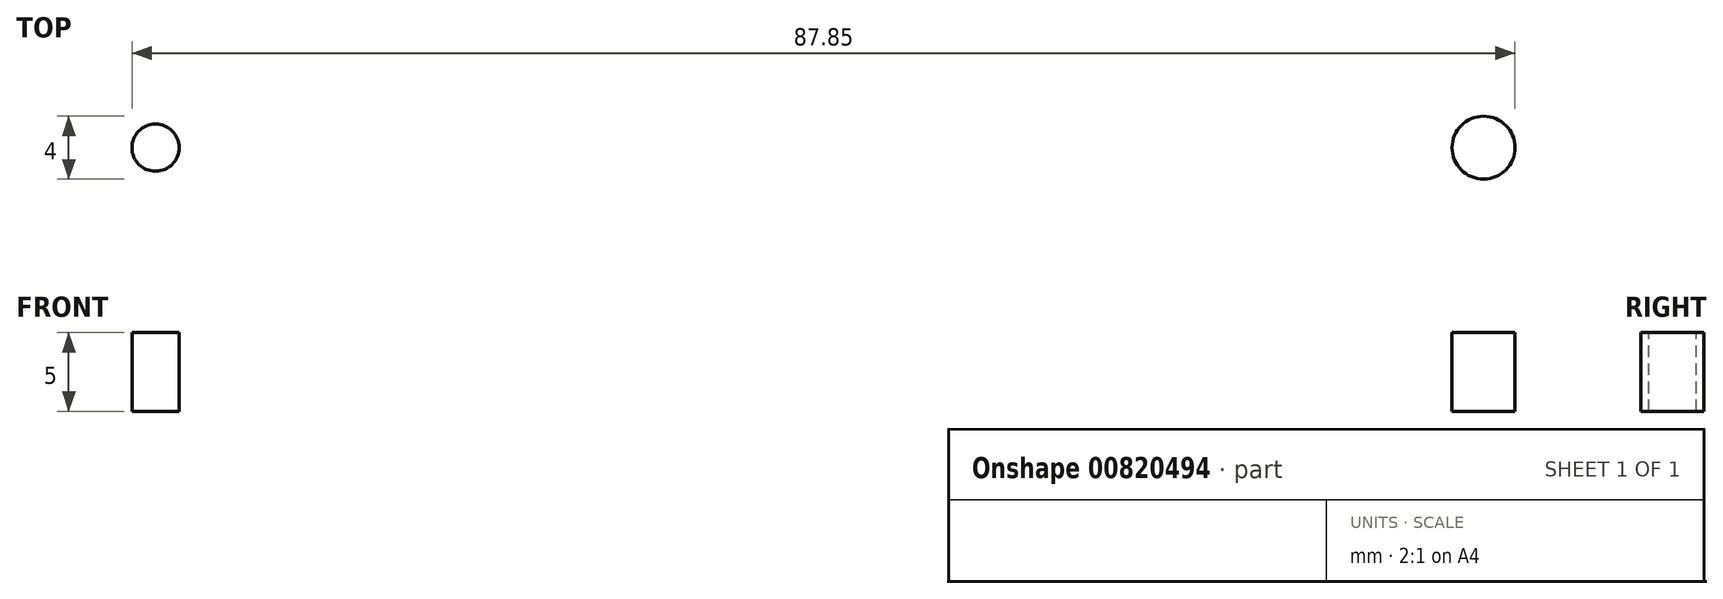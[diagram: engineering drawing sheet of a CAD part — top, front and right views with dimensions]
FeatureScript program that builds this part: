
annotation { "Feature Type Name" : "Feature", "Feature Type Description" : "" }
export const myFeature = defineFeature(function(context is Context, id is Id, definition is map)
    precondition{}
    {
        {
            var Q0;
            Q0=qCreatedBy(makeId("Top.planeOp"),FACE);
            var sketch = newSketch(context, id + "F0", { "sketchPlane" : qUnion([Q0])});
            skLineSegment(sketch, "E0.bottom", {"start": v(69.35, 12.75) * mm, "end": v(-69.35, 12.75) * mm});
            skLineSegment(sketch, "E0.top", {"start": v(69.35, -12.75) * mm, "end": v(-69.35, -12.75) * mm});
            skLineSegment(sketch, "E0.left", {"start": v(69.35, 12.75) * mm, "end": v(69.35, -12.75) * mm});
            skLineSegment(sketch, "E0.right", {"start": v(-69.35, 12.75) * mm, "end": v(-69.35, -12.75) * mm});
            skPoint(sketch, "E0.middle", {"position": v(0, 0) * mm});
            skSolve(sketch);
        }
        {
            var Q0;
            Q0=makeQuery(id+"F0.imprint","IMPRINT",FACE,{"disambiguationData":[TD([[makeQuery(id+"F0.imprint","IMPRINT",EDGE,{"derivedFrom":sQuery(id+"F0.wireOp",EDGE,"E0.bottom")}),1.0]])]});
            extrude(context, id + "F1", {"entities" : qUnion([Q0]), "depth" : 5 * mm, "offsetDistance" : 25 * mm});
        }
        {
            var Q0;
            Q0=makeQuery(id+"F1.opExtrude","CAP_FACE",FACE,{"disambiguationData":[OSD([sQuery(id+"F0.wireOp",EDGE,"E0.bottom"),sQuery(id+"F0.wireOp",EDGE,"E0.top"),sQuery(id+"F0.wireOp",EDGE,"E0.left"),sQuery(id+"F0.wireOp",EDGE,"E0.right")])],"isStart":false});
            var sketch = newSketch(context, id + "F2", { "sketchPlane" : qUnion([Q0])});
            skCircle(sketch, "E1", {"center": v(0, 0) * mm, "radius": 9.5 * mm});
            skSolve(sketch);
        }
        {
            var Q0;
            Q0=makeQuery(id+"F2.imprint","IMPRINT",FACE,{"disambiguationData":[TD([[makeQuery(id+"F2.imprint","IMPRINT",EDGE,{"derivedFrom":sQuery(id+"F2.wireOp",EDGE,"E1")}),1.0]])]});
            extrude(context, id + "F3", {"entities" : qUnion([Q0]), "operationType" : NewBodyOperationType.REMOVE, "oppositeDirection" : true, "depth" : 25 * mm, "offsetDistance" : 25 * mm});
        }
        {
            var Q0;
            Q0=makeQuery(id+"F1.opExtrude","CAP_FACE",FACE,{"disambiguationData":[OSD([sQuery(id+"F0.wireOp",EDGE,"E0.bottom"),sQuery(id+"F0.wireOp",EDGE,"E0.top"),sQuery(id+"F0.wireOp",EDGE,"E0.left"),sQuery(id+"F0.wireOp",EDGE,"E0.right")])],"isStart":false});
            var sketch = newSketch(context, id + "F4", { "sketchPlane" : qUnion([Q0])});
            skCircle(sketch, "E2", {"center": v(0, 0) * mm, "radius": 70.51 * mm});
            skSolve(sketch);
        }
        {
            var Q0;
            Q0=makeQuery(id+"F4.imprint","IMPRINT",FACE,{"disambiguationData":[TD([[makeQuery(id+"F4.imprint","IMPRINT",EDGE,{"derivedFrom":makeQuery(id+"F1.opExtrude","CAP_EDGE",EDGE,{"disambiguationData":[OSD([sQuery(id+"F0.wireOp",EDGE,"E0.bottom")])],"isStart":false})}),1.0]])]});
            var sketch = newSketch(context, id + "F5", { "sketchPlane" : qUnion([Q0])});
            skCircle(sketch, "E3", {"center": v(-64.35, 0) * mm, "radius": 2 * mm});
            skCircle(sketch, "E4.MirrorC", {"center": v(64.35, 0) * mm, "radius": 2 * mm});
            skCircle(sketch, "E5", {"center": v(20, 0) * mm, "radius": 1.5 * mm});
            skCircle(sketch, "E6.MirrorC", {"center": v(-20, 0) * mm, "radius": 1.5 * mm});
            skSolve(sketch);
        }
        {
            var Q0;
            Q0=makeQuery(id+"F5.imprint","IMPRINT",FACE,{"disambiguationData":[TD([[makeQuery(id+"F5.imprint","IMPRINT",EDGE,{"derivedFrom":sQuery(id+"F5.wireOp",EDGE,"E3")}),1.0]])]});
            var Q1;
            Q1=makeQuery(id+"F5.imprint","IMPRINT",FACE,{"disambiguationData":[TD([[makeQuery(id+"F5.imprint","IMPRINT",EDGE,{"derivedFrom":sQuery(id+"F5.wireOp",EDGE,"E4.MirrorC")}),-1.0]])]});
            var Q2;
            Q2=makeQuery(id+"F5.imprint","IMPRINT",FACE,{"disambiguationData":[TD([[makeQuery(id+"F5.imprint","IMPRINT",EDGE,{"derivedFrom":sQuery(id+"F5.wireOp",EDGE,"E5")}),1.0]])]});
            var Q3;
            Q3=makeQuery(id+"F5.imprint","IMPRINT",FACE,{"disambiguationData":[TD([[makeQuery(id+"F5.imprint","IMPRINT",EDGE,{"derivedFrom":sQuery(id+"F5.wireOp",EDGE,"E6.MirrorC")}),-1.0]])]});
            extrude(context, id + "F6", {"entities" : qUnion([Q0, Q1, Q2, Q3]), "operationType" : NewBodyOperationType.REMOVE, "oppositeDirection" : true, "depth" : 25 * mm, "offsetDistance" : 25 * mm});
        }
    });
